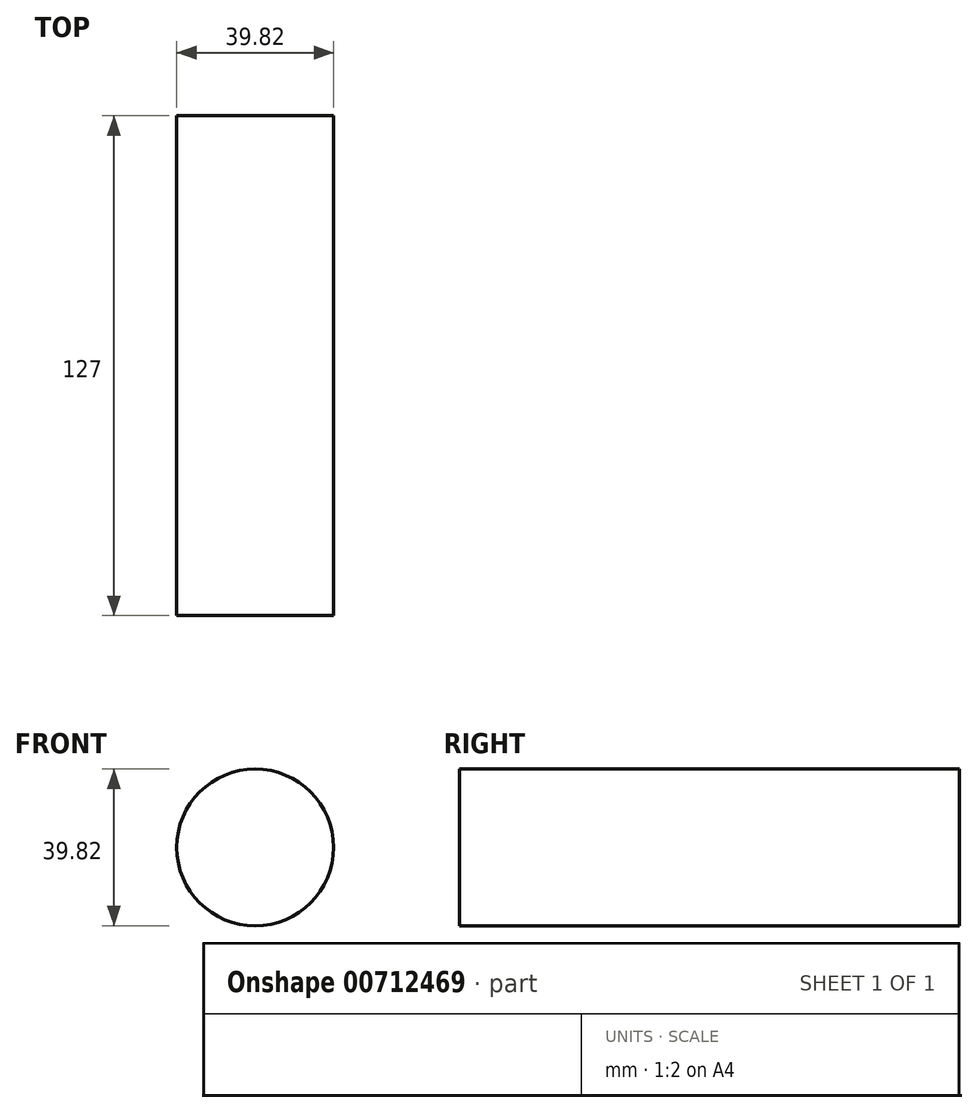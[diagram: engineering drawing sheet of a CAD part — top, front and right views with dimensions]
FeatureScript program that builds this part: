
annotation { "Feature Type Name" : "Feature", "Feature Type Description" : "" }
export const myFeature = defineFeature(function(context is Context, id is Id, definition is map)
    precondition{}
    {
        {
            var Q0;
            Q0=qCreatedBy(makeId("Front.planeOp"),FACE);
            var sketch = newSketch(context, id + "F0", { "sketchPlane" : qUnion([Q0])});
            skCircle(sketch, "E0", {"center": v(0, 0) * mm, "radius": 19.9 * mm});
            skSolve(sketch);
        }
        {
            var Q0;
            Q0=makeQuery(id+"F0.imprint","IMPRINT",FACE,{"disambiguationData":[TD([[makeQuery(id+"F0.imprint","IMPRINT",EDGE,{"derivedFrom":sQuery(id+"F0.wireOp",EDGE,"E0")}),1.0]])]});
            extrude(context, id + "F1", {"entities" : qUnion([Q0]), "depth" : 127 * mm, "offsetDistance" : 25.4 * mm});
        }
    });
